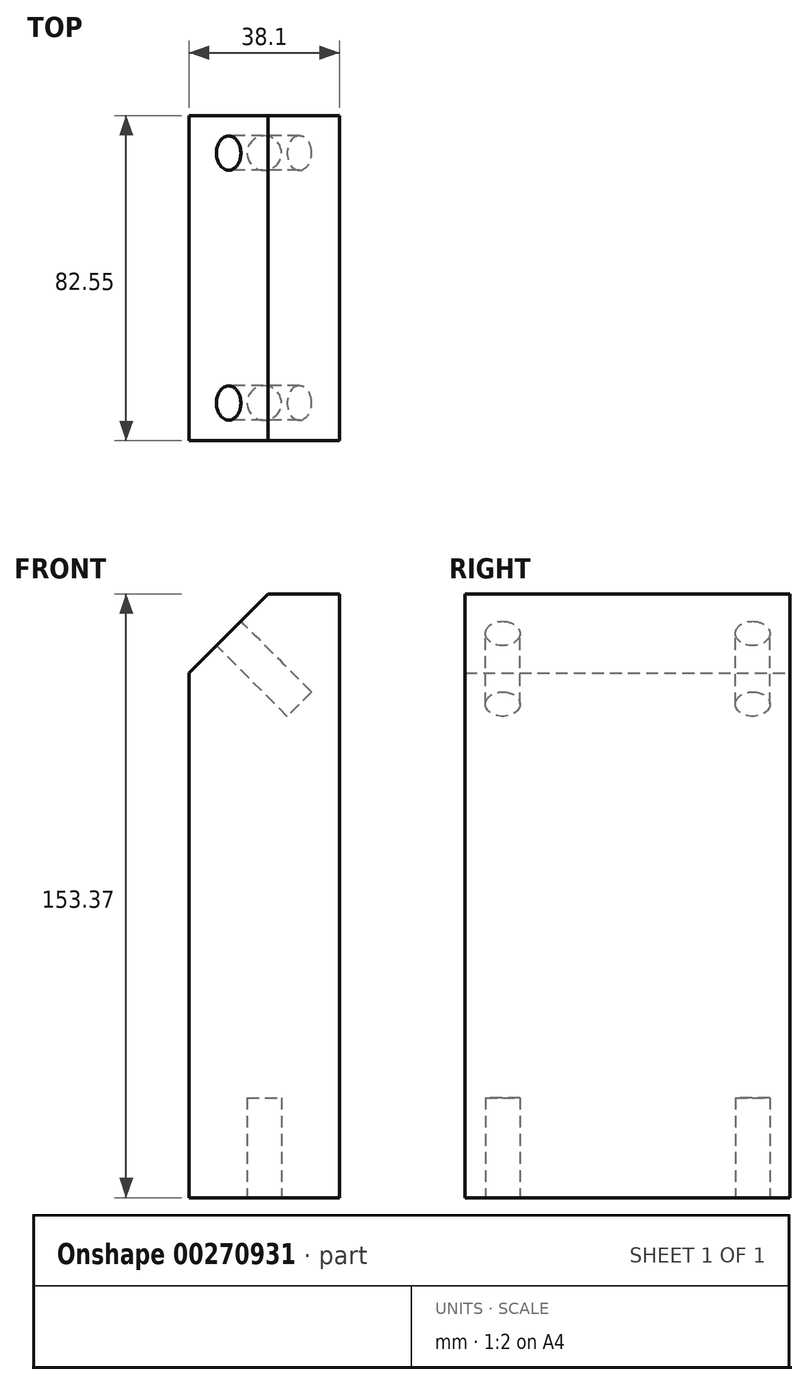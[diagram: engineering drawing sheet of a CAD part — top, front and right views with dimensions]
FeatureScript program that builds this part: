
annotation { "Feature Type Name" : "Feature", "Feature Type Description" : "" }
export const myFeature = defineFeature(function(context is Context, id is Id, definition is map)
    precondition{}
    {
        {
            var Q0;
            Q0=qCreatedBy(makeId("Front.planeOp"),FACE);
            var sketch = newSketch(context, id + "F0", { "sketchPlane" : qUnion([Q0])});
            skLineSegment(sketch, "E0", {"start": v(0, 0) * mm, "end": v(0, 153.37) * mm});
            skLineSegment(sketch, "E1", {"start": v(0, 153.37) * mm, "end": v(-18.08, 153.37) * mm});
            skLineSegment(sketch, "E2", {"start": v(0, 0) * mm, "end": v(-38.1, 0) * mm});
            skLineSegment(sketch, "E3", {"start": v(-38.1, 0) * mm, "end": v(-38.1, 133.35) * mm});
            skLineSegment(sketch, "E4", {"start": v(-18.08, 153.37) * mm, "end": v(-38.1, 133.35) * mm});
            skSolve(sketch);
        }
        {
            var Q0;
            Q0 = qSketchRegion(id + "F0", true);
            extrude(context, id + "F1", {"entities" : qUnion([Q0]), "depth" : 82.55 * mm});
        }
        {
            var Q0;
            Q0=makeQuery(id+"F1.opExtrude","SWEPT_FACE",FACE,{"disambiguationData":[OSD([sQuery(id+"F0.wireOp",EDGE,"E4")])]});
            var sketch = newSketch(context, id + "F2", { "sketchPlane" : qUnion([Q0])});
            skLineSegment(sketch, "E5", {"start": v(0, 95.66) * mm, "end": v(41.28, 95.66) * mm});
            skLineSegment(sketch, "E6", {"start": v(41.28, 95.66) * mm, "end": v(82.55, 95.66) * mm});
            skLineSegment(sketch, "E7", {"start": v(82.55, 95.66) * mm, "end": v(82.55, 81.5) * mm});
            skLineSegment(sketch, "E8", {"start": v(82.55, 81.5) * mm, "end": v(0, 81.5) * mm});
            skLineSegment(sketch, "E9", {"start": v(82.55, 81.5) * mm, "end": v(73.03, 81.5) * mm});
            skLineSegment(sketch, "E10", {"start": v(0, 81.5) * mm, "end": v(9.53, 81.5) * mm});
            skCircle(sketch, "E11", {"center": v(9.53, 81.5) * mm, "radius": 4.37 * mm});
            skCircle(sketch, "E12", {"center": v(73.03, 81.5) * mm, "radius": 4.37 * mm});
            skSolve(sketch);
        }
        {
            var Q0;
            Q0=makeQuery(id+"F1.opExtrude","SWEPT_FACE",FACE,{"disambiguationData":[OSD([sQuery(id+"F0.wireOp",EDGE,"E2")])]});
            var sketch = newSketch(context, id + "F3", { "sketchPlane" : qUnion([Q0])});
            skCircle(sketch, "E13", {"center": v(-19.05, 9.52) * mm, "radius": 4.37 * mm});
            skCircle(sketch, "E14", {"center": v(-19.05, 73.03) * mm, "radius": 4.37 * mm});
            skSolve(sketch);
        }
        {
            var Q0;
            Q0 = qSketchRegion(id + "F3", true);
            extrude(context, id + "F4", {"entities" : qUnion([Q0]), "operationType" : NewBodyOperationType.REMOVE, "oppositeDirection" : true, "depth" : 25.4 * mm});
        }
        {
            var Q0;
            Q0 = qSketchRegion(id + "F2", true);
            extrude(context, id + "F5", {"entities" : qUnion([Q0]), "operationType" : NewBodyOperationType.REMOVE, "oppositeDirection" : true, "depth" : 25.4 * mm});
        }
    });
